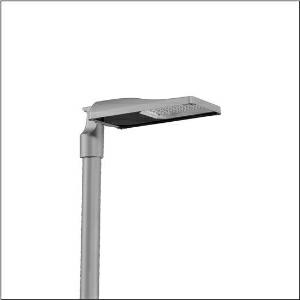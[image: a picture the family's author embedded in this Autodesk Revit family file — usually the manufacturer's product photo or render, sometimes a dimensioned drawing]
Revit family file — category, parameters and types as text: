
# Revit family: streetlight_sl_31_mini___st1_0a_5xh2d3ab08ga_301b
name_source: partatom
category: Lighting Fixtures
units: mm (PartAtom-declared; Revit-internal decimal feet)

## family parameters
Cut with Voids When Loaded = No
Host = Face
Light Source = No
Part Type = Normal
Room Calculation Point = No
Round Connector Dimension = Use Diameter
Shared = No

## types (1)
- --- (1 x LED, 5710 lm, 37.3 W, 3000K)
    Apparent Load = 37 VA
    CIE Flux Codes = 37 72 97 100 100
    Color Rendering = 70
    Color Temperature = 3000K
    Default Elevation = 1800 mm
    Description = Streetlight SL 31 mini Easy LST mast luminaire for post-top, side-entry; light control with lens of PMMA; light distribution: ST1.0a, direct asymmetric distribution, for standard-compliant lighting for roads and squares; LED: luminous flux: 5.710lm, light colour: 730, colour temperature: 3000K; luminous efficacy: 153,1lm/W; control: pre-setting: linear dimming characteristic, flexible luminous flux parameterisation, time-dependent luminous flux control, constant luminous flux control, power reduction, intelligent temperature release in ECG and LED module, overheat protection; luminaire housing, of diecast aluminium, SITECO metallic grey (DB 702S), corrosivity category C5 high according to DIN EN ISO 12944; cover of toughened safety glass, transparent, mast flange of diecast aluminium, SITECO metallic grey (DB 702S), spigot size: 76/60mm, mast flange included unmounted; cable length: 6,5m, connection cable pre-assembled; mains connection: 220..240V, AC, 50/60Hz; power consumption (at start of service life): 37,3W / (at end of service life): 38,7W / (with reduced operation 50%): 17,5W; protection rating (complete): IP66; insulation class (complete): insulation class II (safety insulation); impact resistance: IK10; certification: CE, ENEC, ENEC+, VDE, UKCA; permissible operating ambient temperature for outdoor applications: -40..+50°C; packaging unit: 1 piece

Light Distribution: ST1.0a
    Height = 76 mm
    Lamp = 1 x LED
    Lamp Light Flux = 5710 lm
    Lamp Power = 37.3 W
    Lamp count = 1
    Length = 547 mm
    Luminous efficacy = 153 lm/W
    Manufacturer = Siteco
    ModVariant = No
    Model = 5XH2D3AB08GA
    Number of Poles = 1
    OnlyDefault = Yes
    Power Factor = 1
    Product Name = Streetlight SL 31 mini | ST1.0a
    Product group = mast luminaire | pylon top
    ProductGroupID = 6100
    Protection Class = Protection class II
    Protection Degree = IP 66
    RLX_Detail_Level = 1
    RLX_Emergency_Light_Flux = 0 lm
    RLX_Emergency_Type = 0
    RLX_Emergency_Type_DB = No
    RlxData = <blob elided: 39509 chars, md5=53b92db4>
    Socket = socket
    Standby Power = 0 W
    System Light Flux = 5710 lm
    System Power = 37 W
    Type Comments = factory setting: luminous flux: 100 % | dim-lin: 254 | 386 mA
    Type Image = l_1300326.jpg
    URL = http://relux.com
    VarID = @adj_061689
    Voltage = 0 V
    Weight = 0.00 kg
    Width = 265 mm

## geometry (parser evidence)
native form markers: Blend x4, Sweep x9
no freeform markers — native parametric forms only
